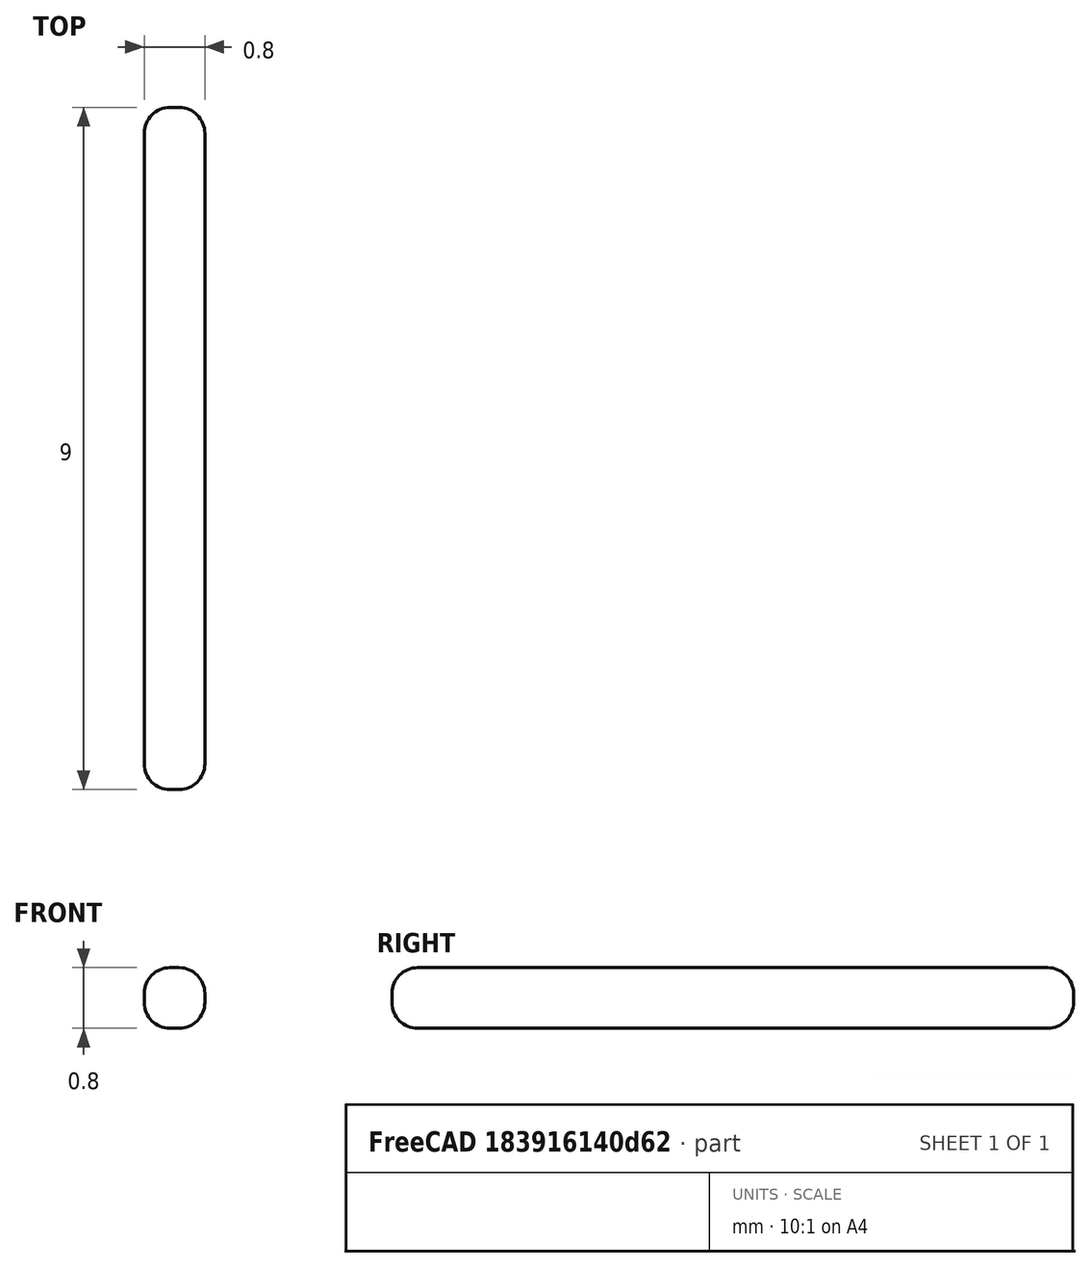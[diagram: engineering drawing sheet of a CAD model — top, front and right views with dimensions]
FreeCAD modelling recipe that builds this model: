
FCSTD DOCUMENT  (FreeCAD 0.16R6712 (Git))
Label: 1
License: All rights reserved
LicenseURL: http://en.wikipedia.org/wiki/All_rights_reserved
objects: Sketcher::SketchObject×1, PartDesign::Pad×1, PartDesign::Fillet×1, Mesh::Feature×1
note: 4 computed .brp shape members not serialized (recipe doc carries the construction recipe); baked Part::Feature solids carry a one-line shape summary decoded from their .brp

FEATURE [Sketcher::SketchObject] Sketch
  sketch-geometry (4):
    g0: LineSegment StartX=-0.4 StartY=0 StartZ=0 EndX=0.4 EndY=0 EndZ=0
    g1: LineSegment StartX=0.4 StartY=0 StartZ=0 EndX=0.4 EndY=9 EndZ=0
    g2: LineSegment StartX=0.4 StartY=9 StartZ=0 EndX=-0.4 EndY=9 EndZ=0
    g3: LineSegment StartX=-0.4 StartY=9 StartZ=0 EndX=-0.4 EndY=0 EndZ=0
  constraints (12):
    c: Coincident(g0,g1)
    c: Coincident(g1,g2)
    c: Coincident(g2,g3)
    c: Coincident(g3,g0)
    c: Horizontal(g0)
    c: Horizontal(g2)
    c: Vertical(g1)
    c: Vertical(g3)
    c: PointOnObject(g-1,g0)
    c: Distance(g1,g0) = 9
    c: Distance(g2,g1) = 0.8
    c: DistanceX(g-2,g0) = 0.4
FEATURE [PartDesign::Pad] Pad
  Length = 0.8
  Length2 = 100
  Midplane = true
  Sketch = -> Sketch
  Type = 0
FEATURE [PartDesign::Fillet] Fillet
  Base = -> Pad [Edge4,Edge7,Edge10,Edge12,Edge8,Edge1,Edge11,Edge3,Edge6,Edge9,Edge2,Edge5]
  Radius = 0.34
FEATURE [Mesh::Feature] Mesh  label="Fillet (Meshed)"
